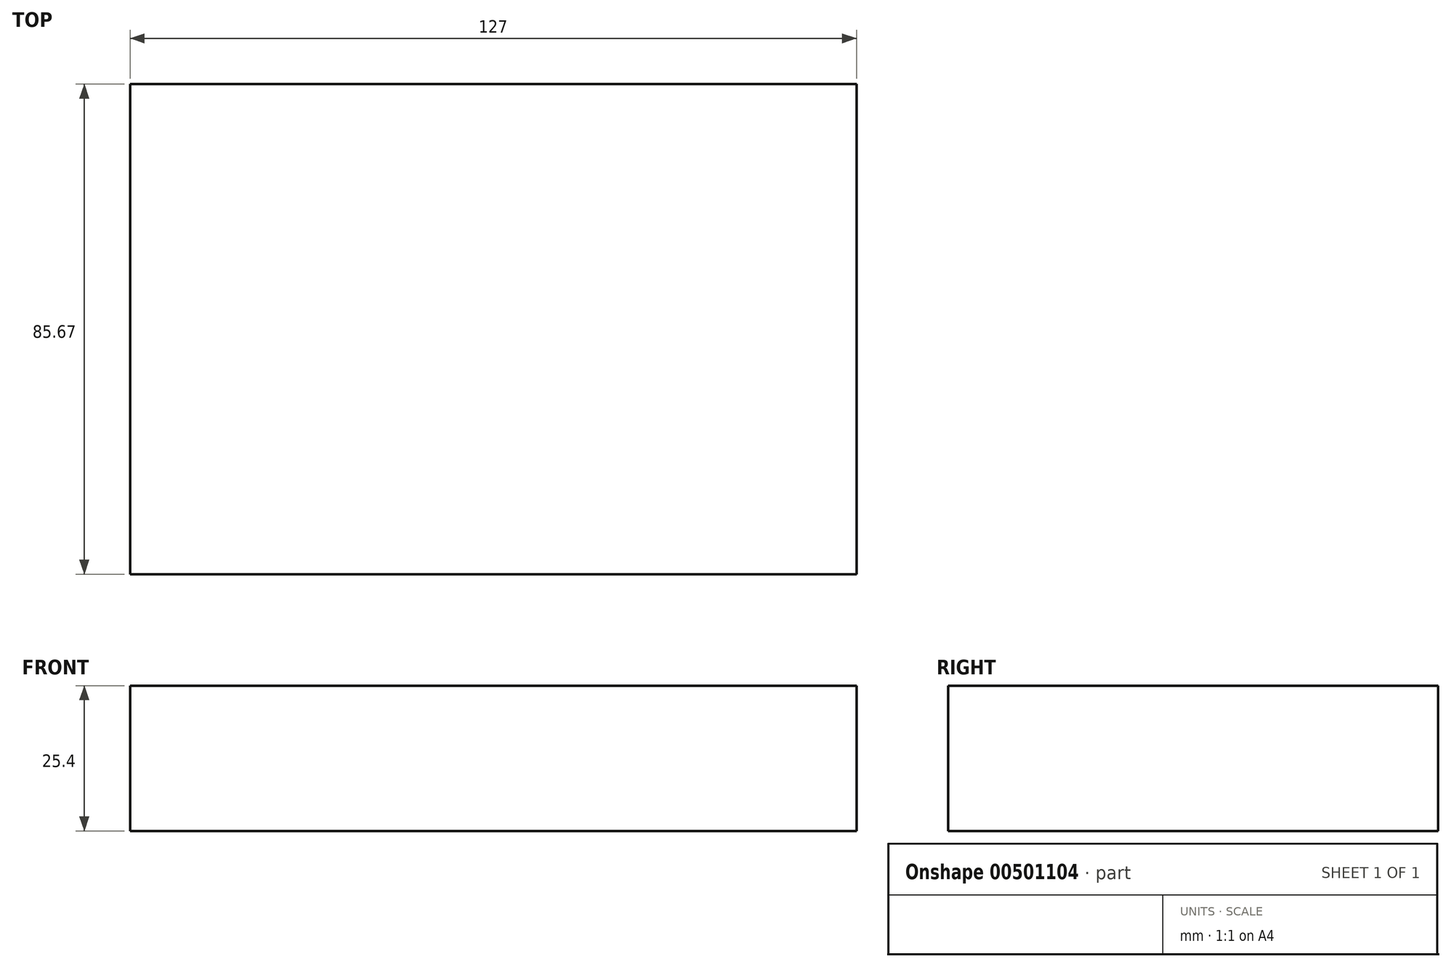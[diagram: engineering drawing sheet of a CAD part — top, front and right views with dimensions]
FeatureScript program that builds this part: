
annotation { "Feature Type Name" : "Feature", "Feature Type Description" : "" }
export const myFeature = defineFeature(function(context is Context, id is Id, definition is map)
    precondition{}
    {
        {
            var Q0;
            Q0=qCreatedBy(makeId("Top.planeOp"),FACE);
            var sketch = newSketch(context, id + "F0", { "sketchPlane" : qUnion([Q0])});
            skLineSegment(sketch, "E0.bottom", {"start": v(-61.6, 41.13) * mm, "end": v(65.4, 41.13) * mm});
            skLineSegment(sketch, "E0.top", {"start": v(-61.6, -44.54) * mm, "end": v(65.4, -44.54) * mm});
            skLineSegment(sketch, "E0.left", {"start": v(-61.6, 41.13) * mm, "end": v(-61.6, -44.54) * mm});
            skLineSegment(sketch, "E0.right", {"start": v(65.4, 41.13) * mm, "end": v(65.4, -44.54) * mm});
            skSolve(sketch);
        }
        {
            var Q0;
            Q0=makeQuery(id+"F0.imprint","IMPRINT",FACE,{"disambiguationData":[TD([[makeQuery(id+"F0.imprint","IMPRINT",EDGE,{"derivedFrom":sQuery(id+"F0.wireOp",EDGE,"E0.bottom")}),-1.0]])]});
            extrude(context, id + "F1", {"entities" : qUnion([Q0]), "depth" : 25.4 * mm});
        }
    });
